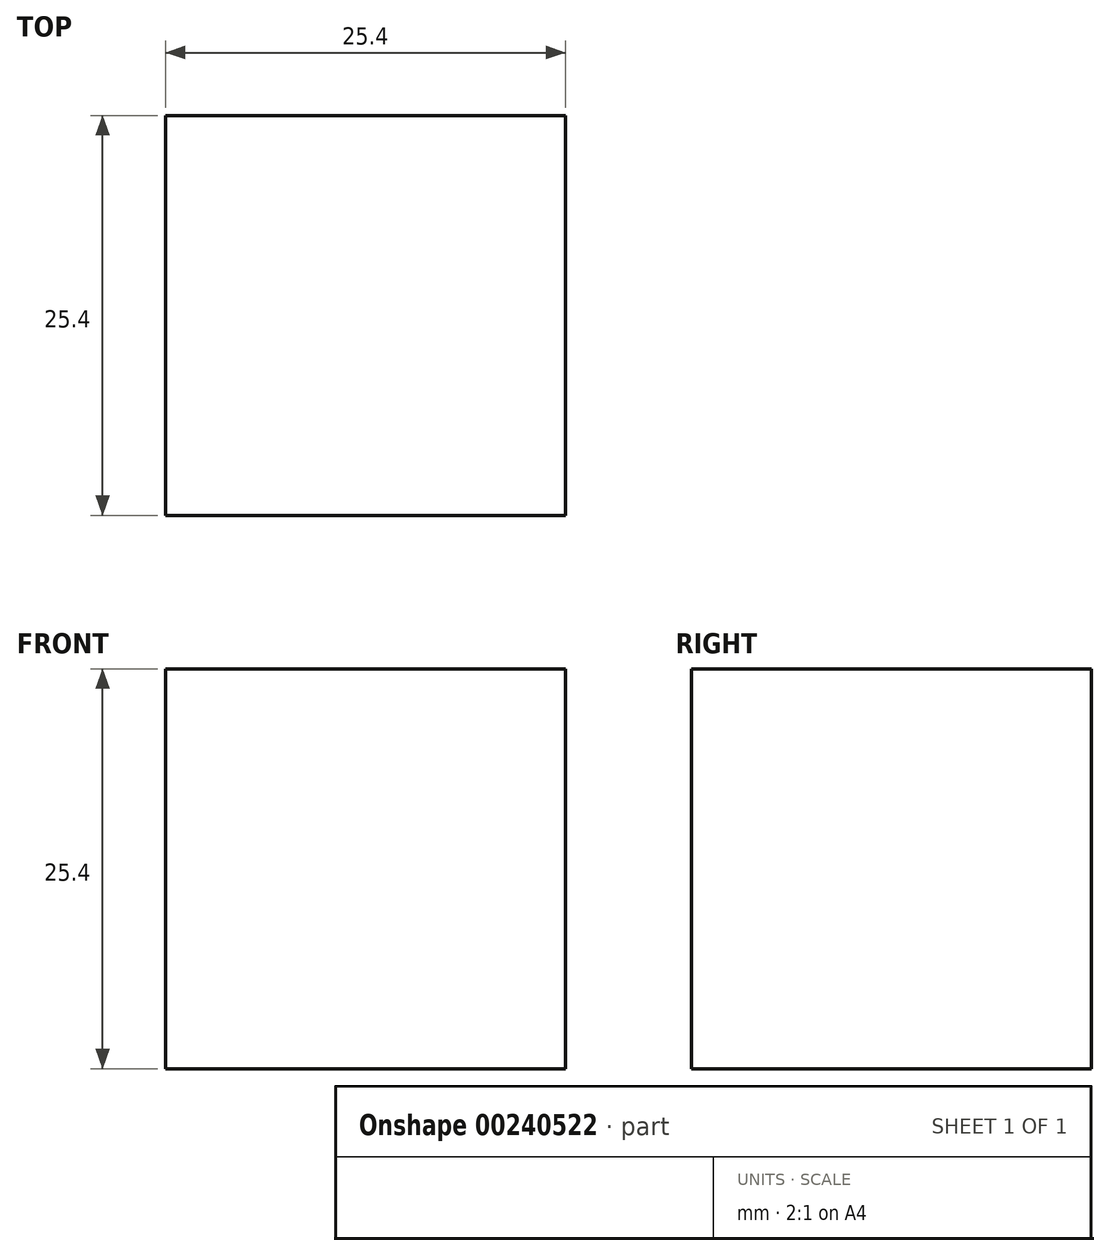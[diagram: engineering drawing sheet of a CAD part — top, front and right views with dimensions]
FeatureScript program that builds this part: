
annotation { "Feature Type Name" : "Feature", "Feature Type Description" : "" }
export const myFeature = defineFeature(function(context is Context, id is Id, definition is map)
    precondition{}
    {
        {
            var Q0;
            Q0=qCreatedBy(makeId("Top.planeOp"),FACE);
            var sketch = newSketch(context, id + "F0", { "sketchPlane" : qUnion([Q0])});
            skLineSegment(sketch, "E0.bottom", {"start": v(0, 0) * mm, "end": v(-25.4, 0) * mm});
            skLineSegment(sketch, "E0.top", {"start": v(0, 25.4) * mm, "end": v(-25.4, 25.4) * mm});
            skLineSegment(sketch, "E0.left", {"start": v(0, 0) * mm, "end": v(0, 25.4) * mm});
            skLineSegment(sketch, "E0.right", {"start": v(-25.4, 0) * mm, "end": v(-25.4, 25.4) * mm});
            skSolve(sketch);
        }
        {
            var Q0;
            Q0 = qSketchRegion(id + "F0", true);
            extrude(context, id + "F1", {"entities" : qUnion([Q0]), "depth" : 25.4 * mm});
        }
    });
